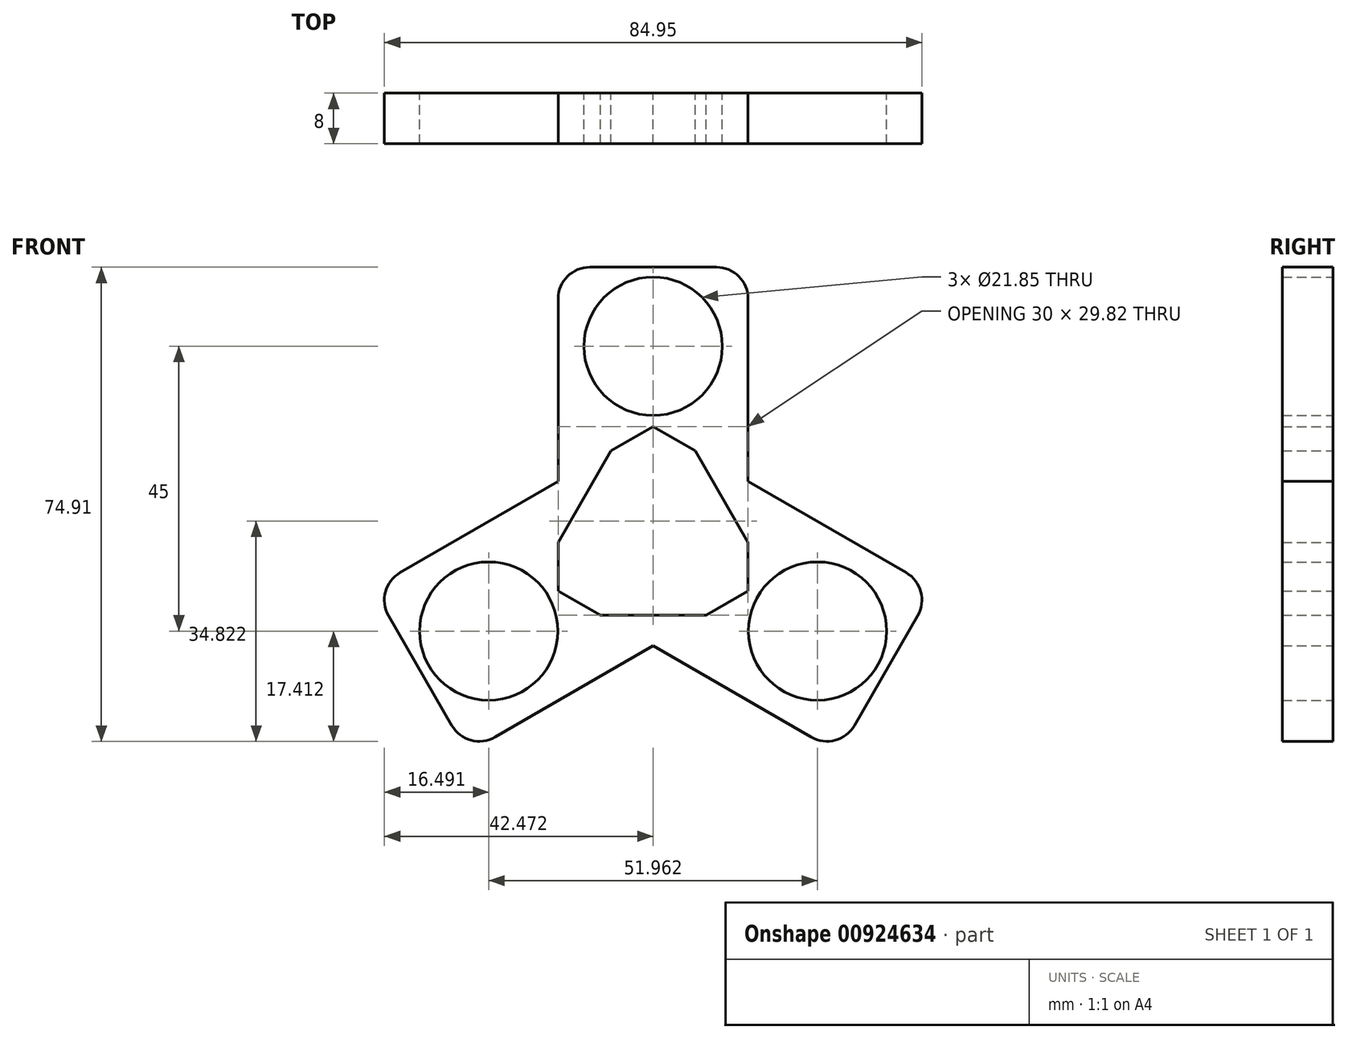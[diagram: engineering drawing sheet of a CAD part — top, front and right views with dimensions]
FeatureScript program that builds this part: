
annotation { "Feature Type Name" : "Feature", "Feature Type Description" : "" }
export const myFeature = defineFeature(function(context is Context, id is Id, definition is map)
    precondition{}
    {
        {
            var Q0;
            Q0=qCreatedBy(makeId("Front.planeOp"),FACE);
            var sketch = newSketch(context, id + "F0", { "sketchPlane" : qUnion([Q0])});
            skCircle(sketch, "E0", {"center": v(-160.86, 0.04) * mm, "radius": 10.93 * mm});
            skCircle(sketch, "E1", {"center": v(-160.86, 30.04) * mm, "radius": 10.93 * mm});
            skLineSegment(sketch, "E2", {"start": v(-160.86, 30.04) * mm, "end": v(-160.86, 0.04) * mm, "construction": true});
            skPoint(sketch, "E3", {"position": v(-160.86, 15.04) * mm});
            skLineSegment(sketch, "E4.bottom", {"start": v(-150.86, 42.54) * mm, "end": v(-170.86, 42.54) * mm});
            skLineSegment(sketch, "E4.top", {"start": v(-145.86, -12.46) * mm, "end": v(-175.86, -12.46) * mm});
            skLineSegment(sketch, "E4.left", {"start": v(-145.86, 37.54) * mm, "end": v(-145.86, -12.46) * mm});
            skLineSegment(sketch, "E4.right", {"start": v(-175.86, 37.54) * mm, "end": v(-175.86, -12.46) * mm});
            skPoint(sketch, "E5.visualSharp", {"position": v(-175.86, 42.54) * mm});
            skArc(sketch, "E5.filletArc", {"start": v(-170.86, 42.54) * mm, "mid": v(-174.4, 41.08) * mm, "end": v(-175.86, 37.54) * mm});
            skPoint(sketch, "E6.visualSharp", {"position": v(-145.86, 42.54) * mm});
            skArc(sketch, "E6.filletArc", {"start": v(-145.86, 37.54) * mm, "mid": v(-147.32, 41.08) * mm, "end": v(-150.86, 42.54) * mm});
            skLineSegment(sketch, "E7.1.1", {"start": v(-200.83, -5.72) * mm, "end": v(-157.53, 19.28) * mm});
            skLineSegment(sketch, "E7.1.2", {"start": v(-157.53, 19.28) * mm, "end": v(-142.53, -6.7) * mm});
            skPoint(sketch, "E7.1.3", {"position": v(-173.85, -7.46) * mm});
            skPoint(sketch, "E7.1.4", {"position": v(-190.16, -34.2) * mm});
            skLineSegment(sketch, "E7.1.5", {"start": v(-186.84, -14.96) * mm, "end": v(-160.86, 0.04) * mm, "construction": true});
            skLineSegment(sketch, "E7.1.6", {"start": v(-185.83, -31.7) * mm, "end": v(-142.53, -6.7) * mm});
            skPoint(sketch, "E7.1.7", {"position": v(-205.16, -8.22) * mm});
            skLineSegment(sketch, "E7.1.8", {"start": v(-202.66, -12.55) * mm, "end": v(-192.66, -29.87) * mm});
            skCircle(sketch, "E7.1.9", {"center": v(-186.84, -14.96) * mm, "radius": 10.93 * mm});
            skPoint(sketch, "E7.1.10", {"position": v(-173.85, -7.46) * mm});
            skArc(sketch, "E7.1.11", {"start": v(-192.66, -29.87) * mm, "mid": v(-189.63, -32.2) * mm, "end": v(-185.83, -31.7) * mm});
            skArc(sketch, "E7.1.12", {"start": v(-200.83, -5.72) * mm, "mid": v(-203.16, -8.75) * mm, "end": v(-202.66, -12.55) * mm});
            skLineSegment(sketch, "E7.2.1", {"start": v(-135.88, -31.7) * mm, "end": v(-179.18, -6.7) * mm});
            skLineSegment(sketch, "E7.2.2", {"start": v(-179.18, -6.7) * mm, "end": v(-164.18, 19.28) * mm});
            skPoint(sketch, "E7.2.3", {"position": v(-147.87, -7.46) * mm});
            skPoint(sketch, "E7.2.4", {"position": v(-116.55, -8.22) * mm});
            skLineSegment(sketch, "E7.2.5", {"start": v(-134.88, -14.96) * mm, "end": v(-160.86, 0.04) * mm, "construction": true});
            skLineSegment(sketch, "E7.2.6", {"start": v(-120.88, -5.72) * mm, "end": v(-164.18, 19.28) * mm});
            skPoint(sketch, "E7.2.7", {"position": v(-131.55, -34.2) * mm});
            skLineSegment(sketch, "E7.2.8", {"start": v(-129.05, -29.87) * mm, "end": v(-119.05, -12.55) * mm});
            skCircle(sketch, "E7.2.9", {"center": v(-134.88, -14.96) * mm, "radius": 10.93 * mm});
            skPoint(sketch, "E7.2.10", {"position": v(-147.87, -7.46) * mm});
            skArc(sketch, "E7.2.11", {"start": v(-119.05, -12.55) * mm, "mid": v(-118.55, -8.75) * mm, "end": v(-120.88, -5.72) * mm});
            skArc(sketch, "E7.2.12", {"start": v(-135.88, -31.7) * mm, "mid": v(-132.09, -32.2) * mm, "end": v(-129.05, -29.87) * mm});
            skSolve(sketch);
        }
        {
            var Q0;
            Q0 = qSketchRegion(id + "F0", true);
            var Q1;
            Q1=makeQuery(id+"F0.imprint","IMPRINT",FACE,{"disambiguationData":[TD([[makeQuery(id+"F0.imprint","IMPRINT",EDGE,{"derivedFrom":sQuery(id+"F0.wireOp",EDGE,"E0")}),-1.0]])]});
            var Q2;
            {var subQ0=sQuery(id+"F0.wireOp",EDGE,"E7.1.2");var subQ1=sQuery(id+"F0.wireOp",EDGE,"E4.left");var subQ2=makeQuery(id+"F0.imprint","INTERSECT",VERTEX,{"derivedFrom":[subQ1,subQ0]});Q2=makeQuery(id+"F0.imprint","IMPRINT",FACE,{"disambiguationData":[TD([[makeQuery(id+"F0.imprint","IMPRINT",EDGE,{"disambiguationData":[TD([[subQ2,-1.0]])],"derivedFrom":subQ1}),1.0]])]});}
            var Q3;
            {var subQ0=sQuery(id+"F0.wireOp",EDGE,"E4.left");var subQ1=sQuery(id+"F0.wireOp",EDGE,"E4.top");var subQ2=makeQuery(id+"F0.imprint","INTERSECT",VERTEX,{"derivedFrom":[subQ1,subQ0]});Q3=makeQuery(id+"F0.imprint","IMPRINT",FACE,{"disambiguationData":[TD([[makeQuery(id+"F0.imprint","IMPRINT",EDGE,{"disambiguationData":[TD([[subQ2,-1.0]])],"derivedFrom":subQ1}),-1.0]])]});}
            var Q4;
            {var subQ0=sQuery(id+"F0.wireOp",EDGE,"E4.right");var subQ1=sQuery(id+"F0.wireOp",EDGE,"E4.top");var subQ2=makeQuery(id+"F0.imprint","INTERSECT",VERTEX,{"derivedFrom":[subQ1,subQ0]});Q4=makeQuery(id+"F0.imprint","IMPRINT",FACE,{"disambiguationData":[TD([[makeQuery(id+"F0.imprint","IMPRINT",EDGE,{"disambiguationData":[TD([[subQ2,1.0]])],"derivedFrom":subQ1}),-1.0]])]});}
            var Q5;
            {var subQ0=sQuery(id+"F0.wireOp",EDGE,"E7.2.2");var subQ1=sQuery(id+"F0.wireOp",EDGE,"E4.right");var subQ2=makeQuery(id+"F0.imprint","INTERSECT",VERTEX,{"derivedFrom":[subQ1,subQ0]});Q5=makeQuery(id+"F0.imprint","IMPRINT",FACE,{"disambiguationData":[TD([[makeQuery(id+"F0.imprint","IMPRINT",EDGE,{"disambiguationData":[TD([[subQ2,-1.0]])],"derivedFrom":subQ1}),-1.0]])]});}
            var Q6;
            {var subQ0=sQuery(id+"F0.wireOp",EDGE,"E7.2.2");var subQ1=sQuery(id+"F0.wireOp",EDGE,"E7.1.1");var subQ2=makeQuery(id+"F0.imprint","INTERSECT",VERTEX,{"derivedFrom":[subQ1,subQ0]});Q6=makeQuery(id+"F0.imprint","IMPRINT",FACE,{"disambiguationData":[TD([[makeQuery(id+"F0.imprint","IMPRINT",EDGE,{"disambiguationData":[TD([[subQ2,-1.0]])],"derivedFrom":subQ1}),1.0]])]});}
            var Q7;
            {var subQ0=sQuery(id+"F0.wireOp",EDGE,"E7.1.2");var subQ1=sQuery(id+"F0.wireOp",EDGE,"E7.1.1");var subQ2=makeQuery(id+"F0.imprint","INTERSECT",VERTEX,{"derivedFrom":[subQ1,subQ0]});Q7=makeQuery(id+"F0.imprint","IMPRINT",FACE,{"disambiguationData":[TD([[makeQuery(id+"F0.imprint","IMPRINT",EDGE,{"disambiguationData":[TD([[subQ2,1.0]])],"derivedFrom":subQ1}),-1.0]])]});}
            extrude(context, id + "F1", {"entities" : qUnion([Q0, Q1, Q2, Q3, Q4, Q5, Q6, Q7]), "depth" : 8 * mm, "offsetDistance" : 25 * mm});
        }
    });
